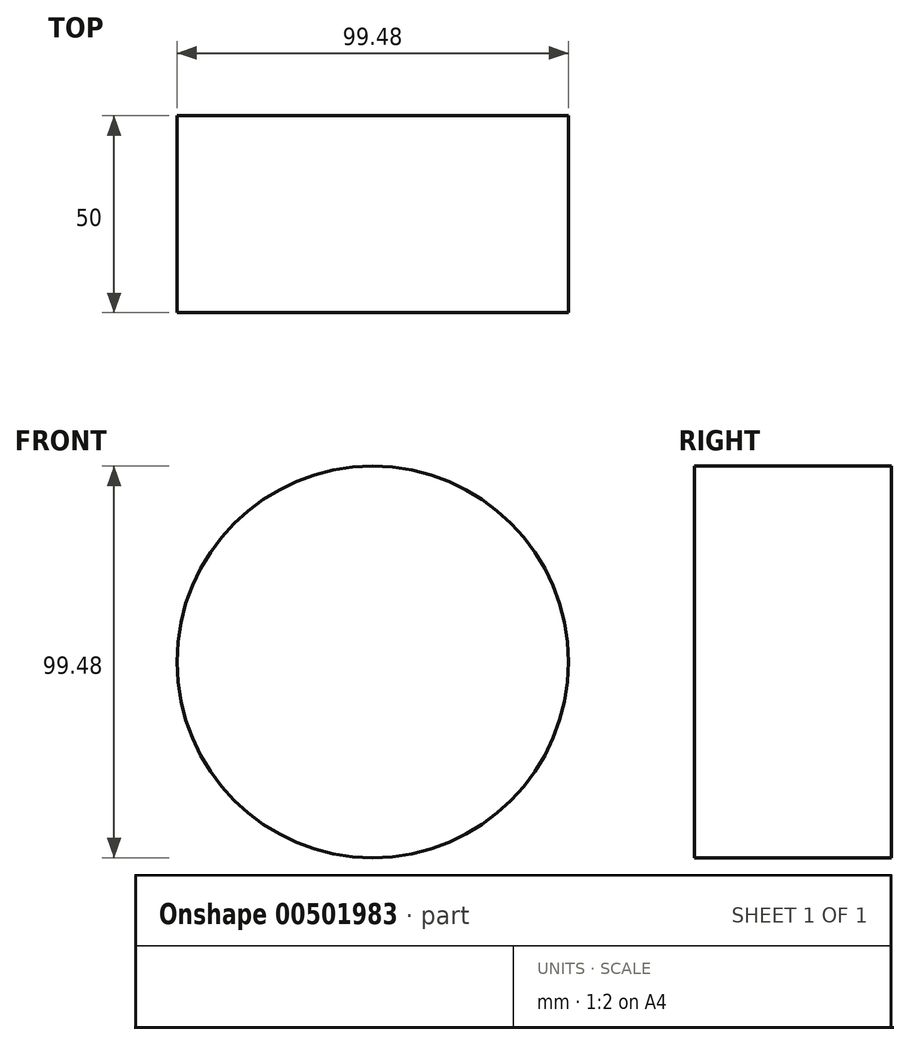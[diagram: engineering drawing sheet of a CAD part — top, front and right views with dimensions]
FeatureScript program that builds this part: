
annotation { "Feature Type Name" : "Feature", "Feature Type Description" : "" }
export const myFeature = defineFeature(function(context is Context, id is Id, definition is map)
    precondition{}
    {
        {
            var Q0;
            Q0=qCreatedBy(makeId("Front.planeOp"),FACE);
            var sketch = newSketch(context, id + "F0", { "sketchPlane" : qUnion([Q0])});
            skCircle(sketch, "E0", {"center": v(0, 0) * mm, "radius": 49.74 * mm});
            skSolve(sketch);
        }
        {
            var Q0;
            Q0=makeQuery(id+"F0.imprint","IMPRINT",FACE,{"disambiguationData":[TD([[makeQuery(id+"F0.imprint","IMPRINT",EDGE,{"derivedFrom":sQuery(id+"F0.wireOp",EDGE,"E0")}),1.0]])]});
            extrude(context, id + "F1", {"entities" : qUnion([Q0]), "endBound" : BoundingType.SYMMETRIC, "depth" : 50 * mm});
        }
    });
